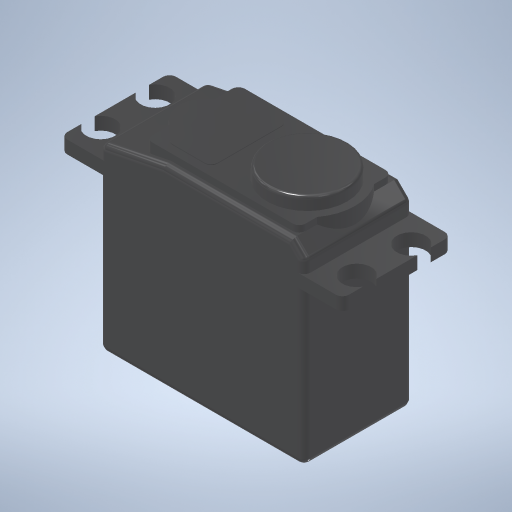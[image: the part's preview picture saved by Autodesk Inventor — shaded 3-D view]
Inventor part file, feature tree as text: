
AUTODESK INVENTOR PART (.ipt)
format: ipt  version: 2023 (Build 270158000, 158)  size: 403,968 bytes
history: native  units: mm
features: extrude x8, fillet x3, chamfer x2, sketch x2
ambient origin geometry x8: Origin, YZ Plane, XZ Plane, XY Plane, X Axis, Y Axis, Z Axis, Center Point
bodies: Volumenkörper1 (feature_tree)
feature tree (15):
  extrude  "Extrusion1"  Depth=17.0mm
  extrude  "Extrusion2"  Depth=0.5mm
  extrude  "Extrusion6"  Depth=30.0mm TaperAngle=0.0deg
  extrude  "Extrusion7"  Depth=0.5mm
  extrude  "Extrusion8"  Depth=8.0mm
  extrude  "Extrusion9"  Depth=3.0mm TaperAngle=0.0deg
  extrude  "Extrusion10"  Depth=2.0mm
  chamfer  "Fase1"  Distance=24.0mm
  chamfer  "Fase2"  Distance=6.0mm
  fillet  "Rundung2"  Radius=2.0mm
  fillet  "Rundung3"  Radius=24.0mm
  extrude  "Extrusion11"  Depth=6.0mm TaperAngle=0.0deg
  fillet  "Rundung4"  Radius=4.5mm
  sketch  "Skizze2"  dims[d0=32.0mm d1=17.0mm]
  sketch  "Skizze10"  dims[d2=8.5mm d3=16.0mm d4=30.0mm d5=0.0mm d6=12.5mm d7=8.0mm d8=3.0mm d9=0.0mm d33=2.0mm d34=24.0mm d35=6.0mm d36=0.0mm d37=2.0mm d38=24.0mm d39=6.0mm d40=0.0mm d41=4.5mm d42=4.5mm d43=4.0mm d44=4.0mm d45=4.25mm d46=4.25mm d47=2.0mm d48=0.0mm d49=4.5mm d50=4.5mm d51=4.25mm d52=4.25mm d53=4.0mm d54=4.0mm d55=2.0mm d56=0.0mm d58=14.5mm d59=24.0mm d60=2.0mm d61=1.25mm d63=1.0mm d64=0.0mm d65=2.0mm d66=10.0mm d67=45.0deg d68=2.0mm d69=2.0mm d70=45.0deg d71=1.0mm d72=1.0mm d73=12.0mm d74=7.0mm d75=2.5mm d76=2.0mm d77=1.0mm d78=0.1mm d79=0.0mm d87=0.5mm]
